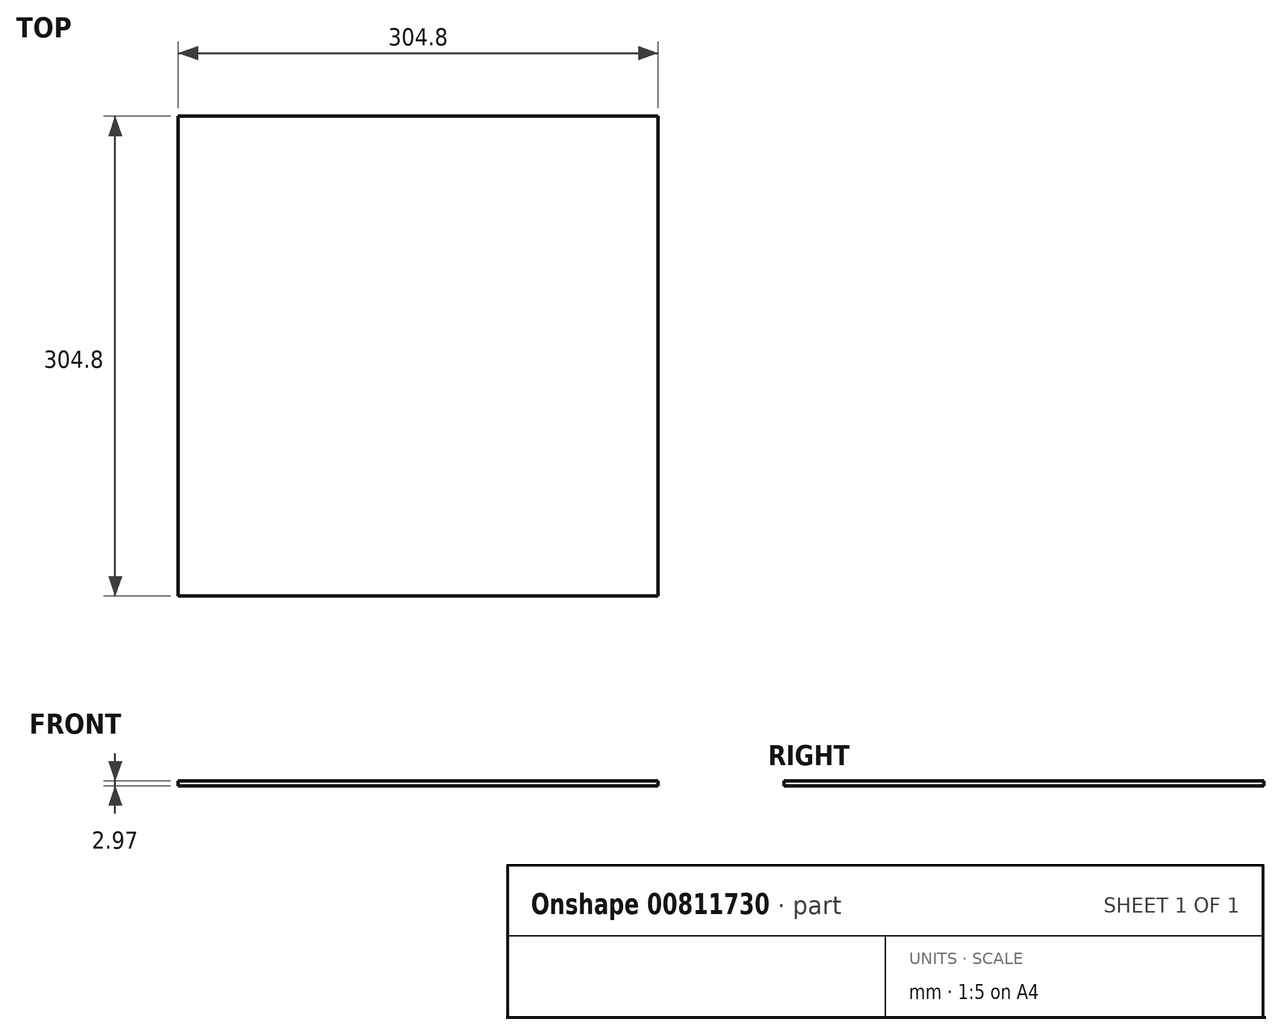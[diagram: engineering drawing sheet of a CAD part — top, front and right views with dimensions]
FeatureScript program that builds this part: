
annotation { "Feature Type Name" : "Feature", "Feature Type Description" : "" }
export const myFeature = defineFeature(function(context is Context, id is Id, definition is map)
    precondition{}
    {
        {
            var Q0;
            Q0=qCreatedBy(makeId("Top.planeOp"),FACE);
            var sketch = newSketch(context, id + "F0", { "sketchPlane" : qUnion([Q0])});
            skLineSegment(sketch, "E0.bottom", {"start": v(152.4, 152.4) * mm, "end": v(-152.4, 152.4) * mm});
            skLineSegment(sketch, "E0.top", {"start": v(152.4, -152.4) * mm, "end": v(-152.4, -152.4) * mm});
            skLineSegment(sketch, "E0.left", {"start": v(152.4, 152.4) * mm, "end": v(152.4, -152.4) * mm});
            skLineSegment(sketch, "E0.right", {"start": v(-152.4, 152.4) * mm, "end": v(-152.4, -152.4) * mm});
            skPoint(sketch, "E0.middle", {"position": v(0, 0) * mm});
            skSolve(sketch);
        }
        {
            var Q0;
            Q0 = qSketchRegion(id + "F0", true);
            extrude(context, id + "F1", {"entities" : qUnion([Q0]), "depth" : 2.97 * mm, "offsetDistance" : 25.4 * mm});
        }
    });
